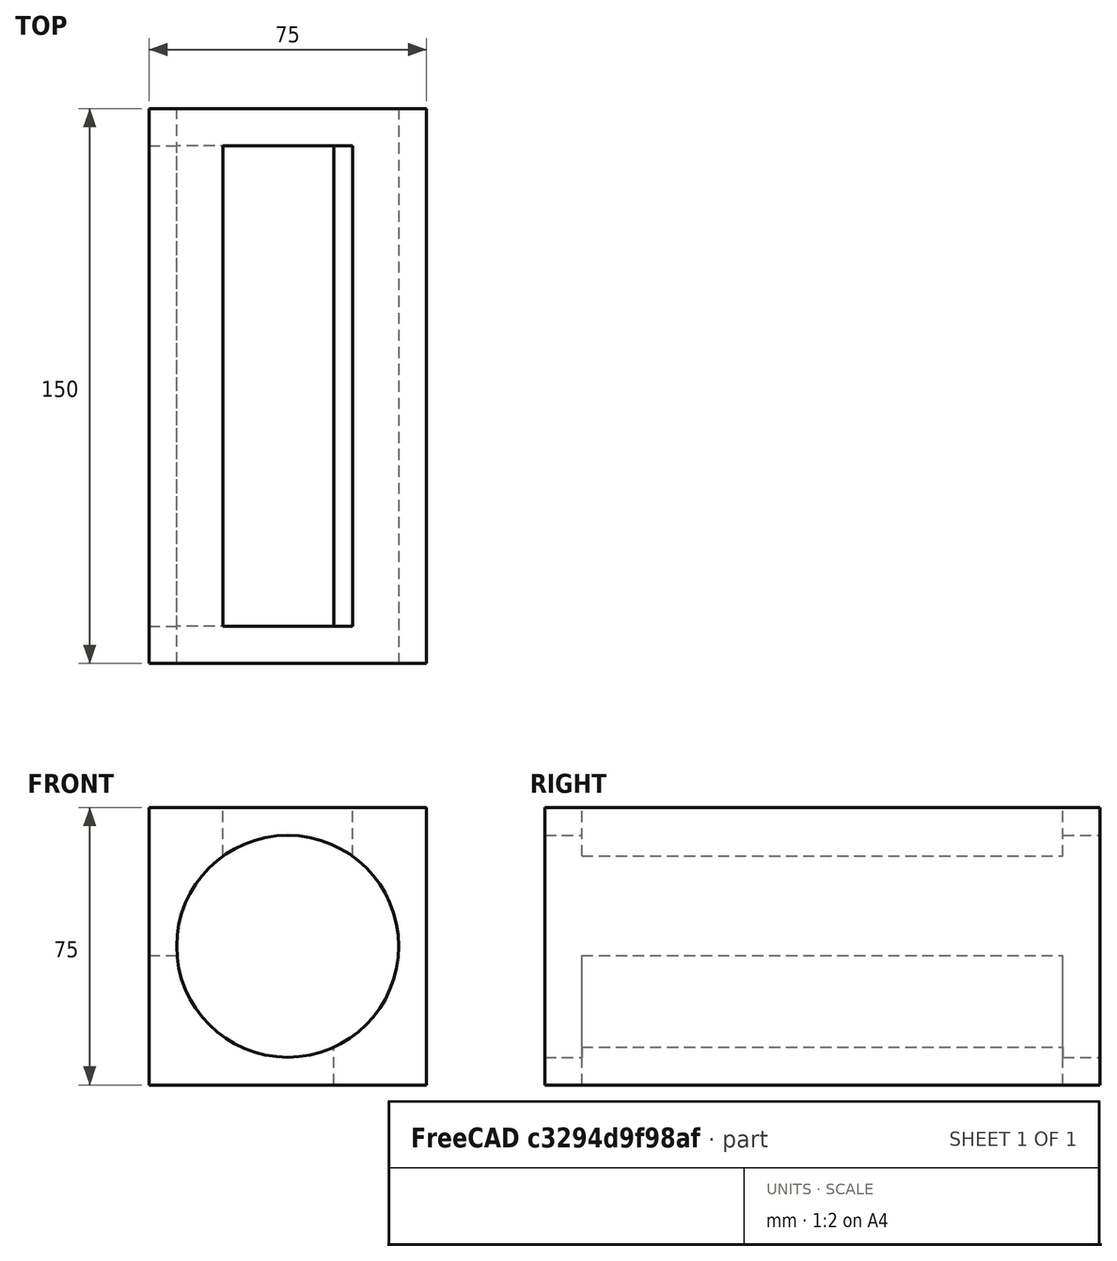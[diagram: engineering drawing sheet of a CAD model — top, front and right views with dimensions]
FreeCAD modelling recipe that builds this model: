
FCSTD DOCUMENT  (FreeCAD 0.20R29603 (Git))
Label: Eisdosierer1
License: All rights reserved
LicenseURL: http://en.wikipedia.org/wiki/All_rights_reserved
objects: TechDraw::DrawViewDimension×15, TechDraw::DrawViewPart×5, PartDesign::SubtractiveBox×2, PartDesign::AdditiveBox×1, PartDesign::SubtractiveCylinder×1, PartDesign::Body×1, TechDraw::DrawSVGTemplate×1, TechDraw::DrawPage×1
note: 9 computed .brp shape members not serialized (recipe doc carries the construction recipe); baked Part::Feature solids carry a one-line shape summary decoded from their .brp

FEATURE [PartDesign::AdditiveBox] Box
  AttacherType = Attacher::AttachEngine3D
  Height = 75
  Length = 75
  Width = 150
FEATURE [PartDesign::SubtractiveCylinder] Cylinder
  Angle = 360
  AttacherType = Attacher::AttachEngine3D
  AttachmentOffset = pos=(37.5,37.5,-150) rot=(0,0,1;0rad)
  BaseFeature = -> Box
  FirstAngle = 0
  Height = 150
  MapMode = 5
  Placement = pos=(37.5,150,37.5) rot=(1,0,0;1.5708rad)
  Radius = 30
  SecondAngle = 0
  Support = -> [Box]
FEATURE [PartDesign::SubtractiveBox] Box001  label="Eingang"
  AttacherType = Attacher::AttachEngine3D
  AttachmentOffset = pos=(20,10,40) rot=(0,0,1;0rad)
  BaseFeature = -> Cylinder
  Height = 35
  Length = 35
  MapMode = 2
  Placement = pos=(20,10,40) rot=(0,0,1;0rad)
  Support = -> [XY_Plane002]
  Width = 130
FEATURE [PartDesign::SubtractiveBox] Box002  label="Ausgang"
  AttacherType = Attacher::AttachEngine3D
  AttachmentOffset = pos=(0,10,0) rot=(0,0,1;0rad)
  BaseFeature = -> Box001
  Height = 35
  Length = 50
  MapMode = 5
  Placement = pos=(0,10,0) rot=(0,0,1;0rad)
  Support = -> [XY_Plane002]
  Width = 130
FEATURE [PartDesign::Body] Body002
  Group = -> [Box,Cylinder,Box001,Box002]
  Origin = -> Origin002
  Tip = -> Box002
FEATURE [TechDraw::DrawSVGTemplate] Template
  EditableTexts = Designed_by_Name=B. Schulze; Drawing_number=1; FC-Date=03.08.2023; FC-SC=1:3; FC-SH=2; FC-Title=Eisdosierer; Subtitle=Dosierer; Weight=0
  Height = 210
  Orientation = 1
  Width = 297
FEATURE [TechDraw::DrawViewPart] View  label="Seite"
  Caption = Seite
  CoarseView = false
  Direction = (0,-1,0)
  Focus = 100
  HardHidden = false
  IsoCount = 0
  IsoHidden = false
  IsoVisible = false
  LockPosition = false
  Perspective = false
  Rotation = 0
  Scale = 0.333333
  ScaleType = 0
  SeamHidden = false
  SeamVisible = true
  SmoothHidden = false
  SmoothVisible = true
  Source = -> [Body002]
  X = 41.3571
  XDirection = (1,0,0)
  Y = 170.357
FEATURE [TechDraw::DrawViewDimension] Dimension
  AngleOverride = false
  Arbitrary = false
  ArbitraryTolerances = false
  EqualTolerance = true
  ExtensionAngle = 0
  FormatSpec = %.2w
  FormatSpecOverTolerance = %+.2w
  FormatSpecUnderTolerance = %+.2w
  Inverted = false
  LineAngle = 0
  LockPosition = false
  MeasureType = 1
  OverTolerance = 0
  References2D = -> [View]
  Rotation = 0
  Scale = 0.333333
  ScaleType = 0
  TheoreticalExact = false
  Type = 2
  UnderTolerance = 0
  X = -22.0589
  Y = 3.0167
FEATURE [TechDraw::DrawViewDimension] Dimension001
  AngleOverride = false
  Arbitrary = false
  ArbitraryTolerances = false
  EqualTolerance = true
  ExtensionAngle = 0
  FormatSpec = %.2w
  FormatSpecOverTolerance = %+.2w
  FormatSpecUnderTolerance = %+.2w
  Inverted = false
  LineAngle = 0
  LockPosition = false
  MeasureType = 1
  OverTolerance = 0
  References2D = -> [View]
  Rotation = 0
  Scale = 0.333333
  ScaleType = 0
  TheoreticalExact = false
  Type = 1
  UnderTolerance = 0
  X = -0.77505
  Y = 23.7839
FEATURE [TechDraw::DrawViewDimension] Dimension002
  AngleOverride = false
  Arbitrary = false
  ArbitraryTolerances = false
  EqualTolerance = true
  ExtensionAngle = 0
  FormatSpec = ⌀%.2w
  FormatSpecOverTolerance = %+.2w
  FormatSpecUnderTolerance = %+.2w
  Inverted = false
  LineAngle = 0
  LockPosition = false
  MeasureType = 1
  OverTolerance = 0
  References2D = -> [View]
  Rotation = 0
  Scale = 0.333333
  ScaleType = 0
  TheoreticalExact = false
  Type = 5
  UnderTolerance = 0
  X = 0
  Y = 0
FEATURE [TechDraw::DrawViewPart] View001  label="Oben"
  Caption = Oben
  CoarseView = false
  Direction = (0,0,1)
  Focus = 100
  HardHidden = false
  IsoCount = 0
  IsoHidden = false
  IsoVisible = false
  LockPosition = false
  Perspective = false
  Rotation = 0
  Scale = 0.333333
  ScaleType = 0
  SeamHidden = false
  SeamVisible = true
  SmoothHidden = false
  SmoothVisible = true
  Source = -> [Body002]
  X = 113.778
  XDirection = (0,-1,0)
  Y = 169.484
FEATURE [TechDraw::DrawViewDimension] Dimension003
  AngleOverride = false
  Arbitrary = false
  ArbitraryTolerances = false
  EqualTolerance = true
  ExtensionAngle = 0
  FormatSpec = %.2w
  FormatSpecOverTolerance = %+.2w
  FormatSpecUnderTolerance = %+.2w
  Inverted = false
  LineAngle = 0
  LockPosition = false
  MeasureType = 1
  OverTolerance = 0
  References2D = -> [View001]
  Rotation = 0
  Scale = 0.333333
  ScaleType = 0
  TheoreticalExact = false
  Type = 1
  UnderTolerance = 0
  X = 0
  Y = 21.6382
FEATURE [TechDraw::DrawViewDimension] Dimension004
  AngleOverride = false
  Arbitrary = false
  ArbitraryTolerances = false
  EqualTolerance = true
  ExtensionAngle = 0
  FormatSpec = %.2w
  FormatSpecOverTolerance = %+.2w
  FormatSpecUnderTolerance = %+.2w
  Inverted = false
  LineAngle = 0
  LockPosition = false
  MeasureType = 1
  OverTolerance = 0
  References2D = -> [View001]
  Rotation = 0
  Scale = 0.333333
  ScaleType = 0
  TheoreticalExact = false
  Type = 2
  UnderTolerance = 0
  X = -34.0422
  Y = 3.14588
FEATURE [TechDraw::DrawViewDimension] Dimension005
  AngleOverride = false
  Arbitrary = false
  ArbitraryTolerances = false
  EqualTolerance = true
  ExtensionAngle = 0
  FormatSpec = %.2w
  FormatSpecOverTolerance = %+.2w
  FormatSpecUnderTolerance = %+.2w
  Inverted = false
  LineAngle = 0
  LockPosition = false
  MeasureType = 1
  OverTolerance = 0
  References2D = -> [View001]
  Rotation = 0
  Scale = 0.333333
  ScaleType = 0
  TheoreticalExact = false
  Type = 2
  UnderTolerance = 0
  X = 30.8382
  Y = 1.026
FEATURE [TechDraw::DrawViewDimension] Dimension006
  AngleOverride = false
  Arbitrary = false
  ArbitraryTolerances = false
  EqualTolerance = true
  ExtensionAngle = 0
  FormatSpec = %.2w
  FormatSpecOverTolerance = %+.2w
  FormatSpecUnderTolerance = %+.2w
  Inverted = false
  LineAngle = 0
  LockPosition = false
  MeasureType = 1
  OverTolerance = 0
  References2D = -> [View001]
  Rotation = 0
  Scale = 0.333333
  ScaleType = 0
  TheoreticalExact = false
  Type = 1
  UnderTolerance = 0
  X = -0.416745
  Y = -23.0435
FEATURE [TechDraw::DrawViewPart] View002  label="Vorne"
  Caption = Vorne
  CoarseView = false
  Direction = (-1,0,0)
  Focus = 100
  HardHidden = false
  IsoCount = 0
  IsoHidden = false
  IsoVisible = false
  LockPosition = false
  Perspective = false
  Rotation = 0
  Scale = 0.333333
  ScaleType = 0
  SeamHidden = false
  SeamVisible = true
  SmoothHidden = false
  SmoothVisible = true
  Source = -> [Body002]
  X = 208.671
  XDirection = (0,-1,0)
  Y = 171.651
FEATURE [TechDraw::DrawViewDimension] Dimension007
  AngleOverride = false
  Arbitrary = false
  ArbitraryTolerances = false
  EqualTolerance = true
  ExtensionAngle = 0
  FormatSpec = %.2w
  FormatSpecOverTolerance = %+.2w
  FormatSpecUnderTolerance = %+.2w
  Inverted = false
  LineAngle = 0
  LockPosition = false
  MeasureType = 1
  OverTolerance = 0
  References2D = -> [View002]
  Rotation = 0
  Scale = 0.333333
  ScaleType = 0
  TheoreticalExact = false
  Type = 1
  UnderTolerance = 0
  X = 3.30176
  Y = 24.4336
FEATURE [TechDraw::DrawViewDimension] Dimension008
  AngleOverride = false
  Arbitrary = false
  ArbitraryTolerances = false
  EqualTolerance = true
  ExtensionAngle = 0
  FormatSpec = %.2w
  FormatSpecOverTolerance = %+.2w
  FormatSpecUnderTolerance = %+.2w
  Inverted = false
  LineAngle = 0
  LockPosition = false
  MeasureType = 1
  OverTolerance = 0
  References2D = -> [View002]
  Rotation = 0
  Scale = 0.333333
  ScaleType = 0
  TheoreticalExact = false
  Type = 2
  UnderTolerance = 0
  X = -38.6787
  Y = 2.26416
FEATURE [TechDraw::DrawViewDimension] Dimension009
  AngleOverride = false
  Arbitrary = false
  ArbitraryTolerances = false
  EqualTolerance = true
  ExtensionAngle = 0
  FormatSpec = %.2w
  FormatSpecOverTolerance = %+.2w
  FormatSpecUnderTolerance = %+.2w
  Inverted = false
  LineAngle = 0
  LockPosition = false
  MeasureType = 1
  OverTolerance = 0
  References2D = -> [View002]
  Rotation = 0
  Scale = 0.333333
  ScaleType = 0
  TheoreticalExact = false
  Type = 1
  UnderTolerance = 0
  X = 0.416745
  Y = -26.2041
FEATURE [TechDraw::DrawViewDimension] Dimension010
  AngleOverride = false
  Arbitrary = false
  ArbitraryTolerances = false
  EqualTolerance = true
  ExtensionAngle = 0
  FormatSpec = %.2w
  FormatSpecOverTolerance = %+.2w
  FormatSpecUnderTolerance = %+.2w
  Inverted = false
  LineAngle = 0
  LockPosition = false
  MeasureType = 1
  OverTolerance = 0
  References2D = -> [View002]
  Rotation = 0
  Scale = 0.333333
  ScaleType = 0
  TheoreticalExact = false
  Type = 2
  UnderTolerance = 0
  X = 31.572
  Y = -2.51579
FEATURE [TechDraw::DrawViewPart] View003  label="Unten"
  Caption = Unten
  CoarseView = false
  Direction = (0,0,-1)
  Focus = 100
  HardHidden = false
  IsoCount = 0
  IsoHidden = false
  IsoVisible = false
  LockPosition = false
  Perspective = false
  Rotation = 0
  Scale = 0.333333
  ScaleType = 0
  SeamHidden = false
  SeamVisible = true
  SmoothHidden = false
  SmoothVisible = true
  Source = -> [Body002]
  X = 59.8914
  XDirection = (0,-1,0)
  Y = 111.994
FEATURE [TechDraw::DrawViewDimension] Dimension011
  AngleOverride = false
  Arbitrary = false
  ArbitraryTolerances = false
  EqualTolerance = true
  ExtensionAngle = 0
  FormatSpec = %.2w
  FormatSpecOverTolerance = %+.2w
  FormatSpecUnderTolerance = %+.2w
  Inverted = false
  LineAngle = 0
  LockPosition = false
  MeasureType = 1
  OverTolerance = 0
  References2D = -> [View003]
  Rotation = 0
  Scale = 0.333333
  ScaleType = 0
  TheoreticalExact = false
  Type = 0
  UnderTolerance = 0
  X = -28.8431
  Y = 7.02549
FEATURE [TechDraw::DrawViewDimension] Dimension012
  AngleOverride = false
  Arbitrary = false
  ArbitraryTolerances = false
  EqualTolerance = true
  ExtensionAngle = 0
  FormatSpec = %.2w
  FormatSpecOverTolerance = %+.2w
  FormatSpecUnderTolerance = %+.2w
  Inverted = false
  LineAngle = 0
  LockPosition = false
  MeasureType = 1
  OverTolerance = 0
  References2D = -> [View003]
  Rotation = 0
  Scale = 0.333333
  ScaleType = 0
  TheoreticalExact = false
  Type = 1
  UnderTolerance = 0
  X = -0.897048
  Y = 23.7911
FEATURE [TechDraw::DrawViewPart] View004  label="Hinten"
  Caption = Hinten
  CoarseView = false
  Direction = (1,0,0)
  Focus = 100
  HardHidden = false
  IsoCount = 0
  IsoHidden = false
  IsoVisible = false
  LockPosition = false
  Perspective = false
  Rotation = 0
  Scale = 0.333333
  ScaleType = 0
  SeamHidden = false
  SeamVisible = true
  SmoothHidden = false
  SmoothVisible = true
  Source = -> [Body002]
  X = 187.582
  XDirection = (0,-1,0)
  Y = 113.164
FEATURE [TechDraw::DrawViewDimension] Dimension013
  AngleOverride = false
  Arbitrary = false
  ArbitraryTolerances = false
  EqualTolerance = true
  ExtensionAngle = 0
  FormatSpec = %.2w
  FormatSpecOverTolerance = %+.2w
  FormatSpecUnderTolerance = %+.2w
  Inverted = false
  LineAngle = 0
  LockPosition = false
  MeasureType = 1
  OverTolerance = 0
  References2D = -> [View004]
  Rotation = 0
  Scale = 0.333333
  ScaleType = 0
  TheoreticalExact = false
  Type = 2
  UnderTolerance = 0
  X = -36.5467
  Y = 1.48117
FEATURE [TechDraw::DrawViewDimension] Dimension014
  AngleOverride = false
  Arbitrary = false
  ArbitraryTolerances = false
  EqualTolerance = true
  ExtensionAngle = 0
  FormatSpec = %.2w
  FormatSpecOverTolerance = %+.2w
  FormatSpecUnderTolerance = %+.2w
  Inverted = false
  LineAngle = 0
  LockPosition = false
  MeasureType = 1
  OverTolerance = 0
  References2D = -> [View004]
  Rotation = 0
  Scale = 0.333333
  ScaleType = 0
  TheoreticalExact = false
  Type = 1
  UnderTolerance = 0
  X = -2.03766
  Y = 21.4526
FEATURE [TechDraw::DrawPage] Page
  KeepUpdated = true
  NextBalloonIndex = 1
  ProjectionType = 0
  Scale = 0.333333
  Template = -> Template
  Views = -> [View,Dimension,Dimension001,Dimension002,View001,Dimension003,Dimension004,Dimension005,Dimension006,View002,Dimension007,Dimension008,Dimension009,Dimension010,View003,Dimension011,Dimension012,View004,Dimension013,Dimension014]
  expr: Scale = 1 / 3
